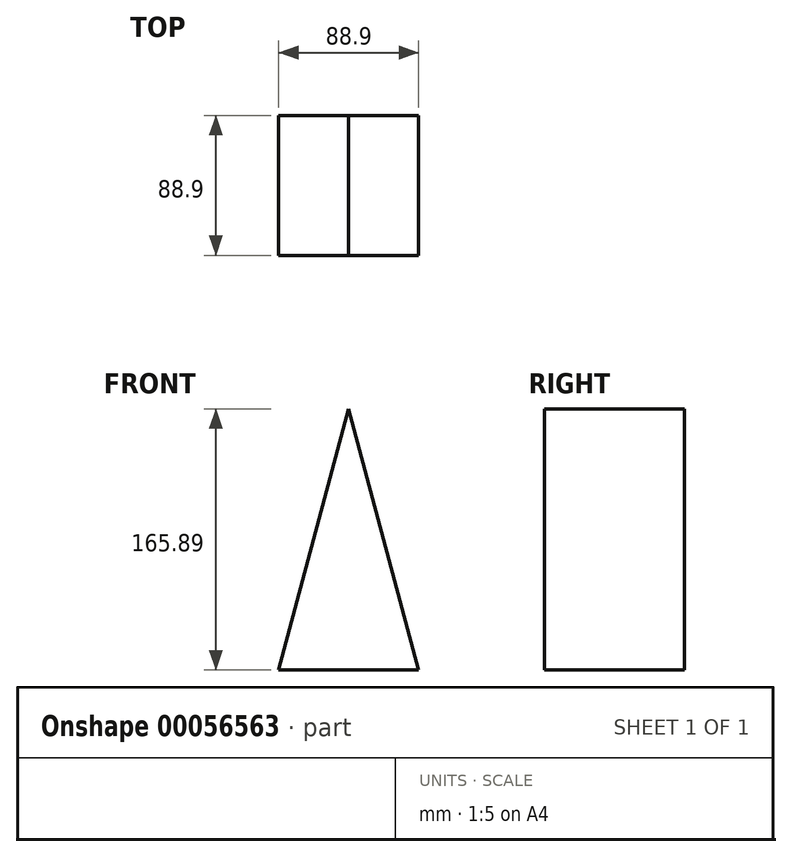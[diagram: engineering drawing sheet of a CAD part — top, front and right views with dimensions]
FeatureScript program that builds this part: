
annotation { "Feature Type Name" : "Feature", "Feature Type Description" : "" }
export const myFeature = defineFeature(function(context is Context, id is Id, definition is map)
    precondition{}
    {
        {
            var Q0;
            Q0=qCreatedBy(makeId("Front.planeOp"),FACE);
            var sketch = newSketch(context, id + "F0", { "sketchPlane" : qUnion([Q0])});
            skLineSegment(sketch, "E0.bottom", {"start": v(-88.9, 165.89) * mm, "end": v(0, 165.89) * mm});
            skLineSegment(sketch, "E0.top", {"start": v(-88.9, 0) * mm, "end": v(0, 0) * mm});
            skLineSegment(sketch, "E0.left", {"start": v(-88.9, 165.89) * mm, "end": v(-88.9, 0) * mm});
            skLineSegment(sketch, "E0.right", {"start": v(0, 165.89) * mm, "end": v(0, 0) * mm});
            skLineSegment(sketch, "E1", {"start": v(-44.45, 165.89) * mm, "end": v(-88.9, 0) * mm});
            skLineSegment(sketch, "E2", {"start": v(-44.45, 165.89) * mm, "end": v(0, 0) * mm});
            skSolve(sketch);
        }
        {
            var Q0;
            Q0=makeQuery(id+"F0.imprint","IMPRINT",FACE,{"disambiguationData":[TD([[makeQuery(id+"F0.imprint","IMPRINT",EDGE,{"derivedFrom":sQuery(id+"F0.wireOp",EDGE,"E0.top")}),1.0]])]});
            extrude(context, id + "F1", {"entities" : qUnion([Q0]), "depth" : 88.9 * mm});
        }
    });
